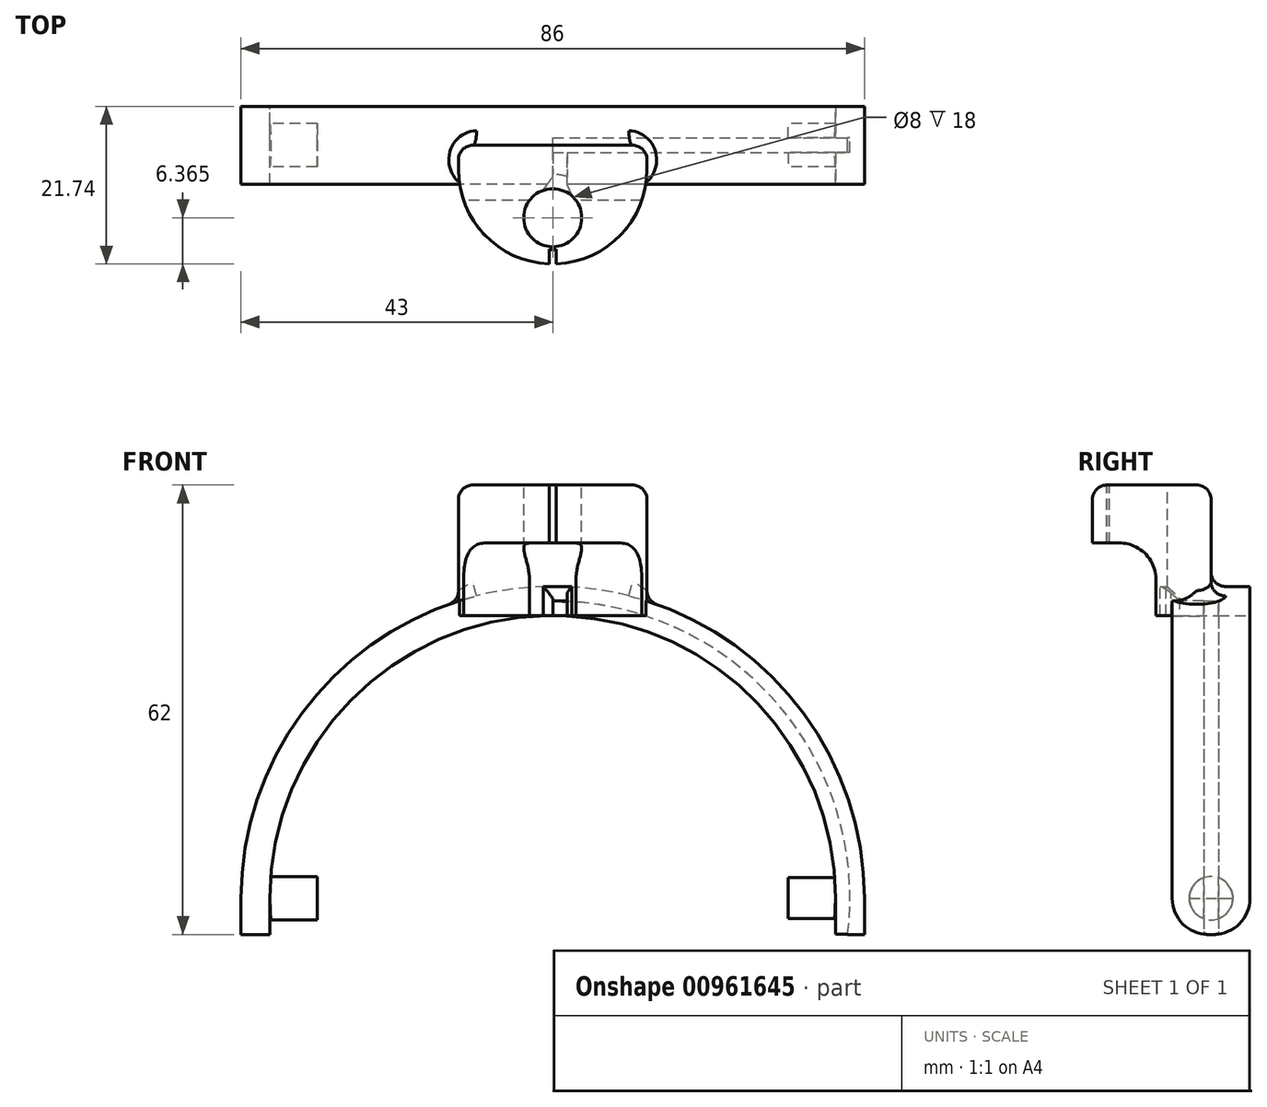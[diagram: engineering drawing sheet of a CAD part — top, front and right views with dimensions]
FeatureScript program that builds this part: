
annotation { "Feature Type Name" : "Feature", "Feature Type Description" : "" }
export const myFeature = defineFeature(function(context is Context, id is Id, definition is map)
    precondition{}
    {
        {
            var Q0;
            Q0=qCreatedBy(makeId("Front.planeOp"),FACE);
            var sketch = newSketch(context, id + "F0", { "sketchPlane" : qUnion([Q0])});
            skArc(sketch, "E0", {"start": v(39, 0) * mm, "mid": v(0, 39) * mm, "end": v(-39, 0) * mm});
            skArc(sketch, "E1", {"start": v(43, 0) * mm, "mid": v(0, 43) * mm, "end": v(-43, 0) * mm});
            skLineSegment(sketch, "E2", {"start": v(-43, 0) * mm, "end": v(-39, 0) * mm});
            skLineSegment(sketch, "E3", {"start": v(39, 0) * mm, "end": v(43, 0) * mm});
            skLineSegment(sketch, "E4", {"start": v(63.06, -5) * mm, "end": v(-58.13, -5) * mm, "construction": true});
            skLineSegment(sketch, "E5", {"start": v(43, 0) * mm, "end": v(43, -5) * mm});
            skLineSegment(sketch, "E6", {"start": v(43, -5) * mm, "end": v(39, -5) * mm});
            skLineSegment(sketch, "E7", {"start": v(39, -5) * mm, "end": v(39, 0) * mm});
            skLineSegment(sketch, "E8", {"start": v(-39, 0) * mm, "end": v(-39, -5) * mm});
            skLineSegment(sketch, "E9", {"start": v(-39, -5) * mm, "end": v(-43, -5) * mm});
            skLineSegment(sketch, "E10", {"start": v(-43, -5) * mm, "end": v(-43, 0) * mm});
            skSolve(sketch);
        }
        {
            var Q0;
            Q0=makeQuery(id+"F0.imprint","IMPRINT",FACE,{"disambiguationData":[TD([[makeQuery(id+"F0.imprint","IMPRINT",EDGE,{"derivedFrom":sQuery(id+"F0.wireOp",EDGE,"E0")}),-1.0]])]});
            var Q1;
            Q1=makeQuery(id+"F0.imprint","IMPRINT",FACE,{"disambiguationData":[TD([[makeQuery(id+"F0.imprint","IMPRINT",EDGE,{"derivedFrom":sQuery(id+"F0.wireOp",EDGE,"E3")}),-1.0]])]});
            var Q2;
            Q2=makeQuery(id+"F0.imprint","IMPRINT",FACE,{"disambiguationData":[TD([[makeQuery(id+"F0.imprint","IMPRINT",EDGE,{"derivedFrom":sQuery(id+"F0.wireOp",EDGE,"E2")}),-1.0]])]});
            extrude(context, id + "F1", {"entities" : qUnion([Q0, Q1, Q2]), "depth" : 10.75 * mm, "offsetDistance" : 25 * mm});
        }
        {
            var Q0;
            Q0=makeQuery(id+"F1.opExtrude","CAP_FACE",FACE,{"disambiguationData":[OSD([sQuery(id+"F0.wireOp",EDGE,"E0"),sQuery(id+"F0.wireOp",EDGE,"E1"),sQuery(id+"F0.wireOp",EDGE,"E2"),sQuery(id+"F0.wireOp",EDGE,"E3")])],"isStart":false});
            var sketch = newSketch(context, id + "F2", { "sketchPlane" : qUnion([Q0])});
            skLineSegment(sketch, "E11.bottom", {"start": v(-13, 57) * mm, "end": v(13, 57) * mm});
            skLineSegment(sketch, "E11.top", {"start": v(-13, 39) * mm, "end": v(13, 39) * mm});
            skLineSegment(sketch, "E11.left", {"start": v(-13, 57) * mm, "end": v(-13, 39) * mm});
            skLineSegment(sketch, "E11.right", {"start": v(13, 57) * mm, "end": v(13, 39) * mm});
            skSolve(sketch);
        }
        {
            var Q0;
            {var subQ0=sQuery(id+"F2.wireOp",EDGE,"E11.bottom");Q0=makeQuery(id+"F2.imprint","IMPRINT",FACE,{"disambiguationData":[TD([[makeQuery(id+"F2.imprint","IMPRINT",EDGE,{"derivedFrom":subQ0}),-1.0]])]});}
            var Q1;
            {var subQ0=sQuery(id+"F2.wireOp",EDGE,"E11.left");var subQ1=sQuery(id+"F2.wireOp",EDGE,"E11.top");var subQ2=makeQuery(id+"F2.imprint","INTERSECT",VERTEX,{"derivedFrom":[subQ1,subQ0]});Q1=makeQuery(id+"F2.imprint","IMPRINT",FACE,{"disambiguationData":[TD([[makeQuery(id+"F2.imprint","IMPRINT",EDGE,{"disambiguationData":[TD([[subQ2,-1.0]])],"derivedFrom":subQ1}),1.0]])]});}
            extrude(context, id + "F3", {"entities" : qUnion([Q0, Q1]), "operationType" : NewBodyOperationType.ADD, "depth" : 11 * mm, "offsetDistance" : 25 * mm, "hasSecondDirection" : true, "secondDirectionOppositeDirection" : true, "secondDirectionDepth" : 5.38 * mm});
        }
        {
            var Q0;
            Q0=makeQuery(id+"F3.opExtrude","CAP_EDGE",EDGE,{"disambiguationData":[OSD([sQuery(id+"F2.wireOp",EDGE,"E11.right")])],"isStart":false});
            var Q1;
            Q1=makeQuery(id+"F3.opExtrude","CAP_EDGE",EDGE,{"disambiguationData":[OSD([sQuery(id+"F2.wireOp",EDGE,"E11.left")])],"isStart":false});
            fillet(context, id + "F4", {"entities" : qUnion([Q0, Q1]), "radius" : 13 * mm, "tangentPropagation" : true, "defaultsChanged" : false, "vertexSettings" : [], "allowEdgeOverflow" : false});
        }
        {
            var Q0;
            Q0=makeQuery(id+"F3.opExtrude","SWEPT_FACE",FACE,{"disambiguationData":[OSD([sQuery(id+"F2.wireOp",EDGE,"E11.bottom")])]});
            var sketch = newSketch(context, id + "F5", { "sketchPlane" : qUnion([Q0])});
            skCircle(sketch, "E12", {"center": v(0, -15.38) * mm, "radius": 4 * mm});
            skSolve(sketch);
        }
        {
            var Q0;
            Q0=makeQuery(id+"F5.imprint","IMPRINT",FACE,{"disambiguationData":[TD([[makeQuery(id+"F5.imprint","IMPRINT",EDGE,{"derivedFrom":sQuery(id+"F5.wireOp",EDGE,"E12")}),1.0]])]});
            extrude(context, id + "F6", {"entities" : qUnion([Q0]), "operationType" : NewBodyOperationType.REMOVE, "oppositeDirection" : true, "depth" : 25 * mm, "offsetDistance" : 25 * mm});
        }
        {
            var Q0;
            {var subQ0=makeQuery(id+"F1.opExtrude","SWEPT_FACE",FACE,{"disambiguationData":[OSD([sQuery(id+"F0.wireOp",EDGE,"E1")])]});var subQ1=sQuery(id+"F2.wireOp",EDGE,"E11.left");var subQ2=makeQuery(id+"F3.opExtrude","CAP_FACE",FACE,{"disambiguationData":[OSD([sQuery(id+"F2.wireOp",EDGE,"E11.bottom"),sQuery(id+"F2.wireOp",EDGE,"E11.top"),subQ1,sQuery(id+"F2.wireOp",EDGE,"E11.right")])],"isStart":true});Q0=makeQuery(id+"FzuqFp6sAI3lxhp_1.boolean.opBoolean","SPLIT",EDGE,{"disambiguationData":[TD([makeQuery(id+"F3.opExtrude","SWEPT_FACE",FACE,{"disambiguationData":[OSD([subQ1])]})])],"derivedFrom":makeQuery(id+"F3.boolean.opBoolean","INTERSECT",EDGE,{"derivedFrom":[subQ0,subQ2]})});}
            var Q1;
            {var subQ0=makeQuery(id+"F1.opExtrude","SWEPT_FACE",FACE,{"disambiguationData":[OSD([sQuery(id+"F0.wireOp",EDGE,"E1")])]});var subQ1=sQuery(id+"F2.wireOp",EDGE,"E11.right");var subQ2=makeQuery(id+"F3.opExtrude","CAP_FACE",FACE,{"disambiguationData":[OSD([sQuery(id+"F2.wireOp",EDGE,"E11.bottom"),sQuery(id+"F2.wireOp",EDGE,"E11.top"),sQuery(id+"F2.wireOp",EDGE,"E11.left"),subQ1])],"isStart":true});Q1=makeQuery(id+"FzuqFp6sAI3lxhp_1.boolean.opBoolean","SPLIT",EDGE,{"disambiguationData":[TD([makeQuery(id+"F3.opExtrude","SWEPT_FACE",FACE,{"disambiguationData":[OSD([subQ1])]})])],"derivedFrom":makeQuery(id+"F3.boolean.opBoolean","INTERSECT",EDGE,{"derivedFrom":[subQ0,subQ2]})});}
            var Q2;
            Q2=makeQuery(id+"FzuqFp6sAI3lxhp_1.boolean.opBoolean","INTERSECT",EDGE,{"derivedFrom":[makeQuery(id+"F3.opExtrude","CAP_FACE",FACE,{"disambiguationData":[OSD([sQuery(id+"F2.wireOp",EDGE,"E11.bottom"),sQuery(id+"F2.wireOp",EDGE,"E11.top"),sQuery(id+"F2.wireOp",EDGE,"E11.left"),sQuery(id+"F2.wireOp",EDGE,"E11.right")])],"isStart":true}),makeQuery(id+"FzuqFp6sAI3lxhp_1.opExtrude","SWEPT_FACE",FACE,{"disambiguationData":[OSD([sQuery(id+"FRsUaT8Pyvrhzy0_1.wireOp",EDGE,"mObt9MSs-sKAg-swzv-7bB1-zA0te2DPEE11.right")])]})]});
            var Q3;
            Q3=makeQuery(id+"FzuqFp6sAI3lxhp_1.boolean.opBoolean","INTERSECT",EDGE,{"derivedFrom":[makeQuery(id+"F3.opExtrude","CAP_FACE",FACE,{"disambiguationData":[OSD([sQuery(id+"F2.wireOp",EDGE,"E11.bottom"),sQuery(id+"F2.wireOp",EDGE,"E11.top"),sQuery(id+"F2.wireOp",EDGE,"E11.left"),sQuery(id+"F2.wireOp",EDGE,"E11.right")])],"isStart":true}),makeQuery(id+"FzuqFp6sAI3lxhp_1.opExtrude","SWEPT_FACE",FACE,{"disambiguationData":[OSD([sQuery(id+"FRsUaT8Pyvrhzy0_1.wireOp",EDGE,"mObt9MSs-sKAg-swzv-7bB1-zA0te2DPEE11.top")])]})]});
            var Q4;
            Q4=makeQuery(id+"FzuqFp6sAI3lxhp_1.boolean.opBoolean","INTERSECT",EDGE,{"derivedFrom":[makeQuery(id+"F3.opExtrude","CAP_FACE",FACE,{"disambiguationData":[OSD([sQuery(id+"F2.wireOp",EDGE,"E11.bottom"),sQuery(id+"F2.wireOp",EDGE,"E11.top"),sQuery(id+"F2.wireOp",EDGE,"E11.left"),sQuery(id+"F2.wireOp",EDGE,"E11.right")])],"isStart":true}),makeQuery(id+"FzuqFp6sAI3lxhp_1.opExtrude","SWEPT_FACE",FACE,{"disambiguationData":[OSD([sQuery(id+"FRsUaT8Pyvrhzy0_1.wireOp",EDGE,"mObt9MSs-sKAg-swzv-7bB1-zA0te2DPEE11.left")])]})]});
            var Q5;
            Q5=makeQuery(id+"F3.opExtrude","CAP_EDGE",EDGE,{"disambiguationData":[OSD([sQuery(id+"F2.wireOp",EDGE,"E11.left")])],"isStart":true});
            var Q6;
            Q6=makeQuery(id+"F4.opFillet","BLEND_EDGE",EDGE,{"blendedFrom":[makeQuery(id+"F3.opExtrude","CAP_EDGE",EDGE,{"disambiguationData":[OSD([sQuery(id+"F2.wireOp",EDGE,"E11.left")])],"isStart":false}),makeQuery(id+"F3.opExtrude","SWEPT_FACE",FACE,{"disambiguationData":[OSD([sQuery(id+"F2.wireOp",EDGE,"E11.bottom")])]})],"blendedInto":[makeQuery(id+"F3.opExtrude","SWEPT_FACE",FACE,{"disambiguationData":[OSD([sQuery(id+"F2.wireOp",EDGE,"E11.bottom")])]})]});
            var Q7;
            Q7=makeQuery(id+"F3.opExtrude","CAP_EDGE",EDGE,{"disambiguationData":[OSD([sQuery(id+"F2.wireOp",EDGE,"E11.bottom")])],"isStart":true});
            var Q8;
            Q8=makeQuery(id+"F3.opExtrude","CAP_EDGE",EDGE,{"disambiguationData":[OSD([sQuery(id+"F2.wireOp",EDGE,"E11.right")])],"isStart":true});
            var Q9;
            Q9=makeQuery(id+"F4.opFillet","BLEND_EDGE",EDGE,{"blendedFrom":[makeQuery(id+"F3.opExtrude","CAP_EDGE",EDGE,{"disambiguationData":[OSD([sQuery(id+"F2.wireOp",EDGE,"E11.right")])],"isStart":false}),makeQuery(id+"FzuqFp6sAI3lxhp_1.boolean.opBoolean","COPY",FACE,{"derivedFrom":makeQuery(id+"FzuqFp6sAI3lxhp_1.opExtrude","SWEPT_FACE",FACE,{"disambiguationData":[OSD([sQuery(id+"FRsUaT8Pyvrhzy0_1.wireOp",EDGE,"mObt9MSs-sKAg-swzv-7bB1-zA0te2DPEE11.top")])]})})],"blendedInto":[makeQuery(id+"FzuqFp6sAI3lxhp_1.boolean.opBoolean","COPY",FACE,{"derivedFrom":makeQuery(id+"FzuqFp6sAI3lxhp_1.opExtrude","SWEPT_FACE",FACE,{"disambiguationData":[OSD([sQuery(id+"FRsUaT8Pyvrhzy0_1.wireOp",EDGE,"mObt9MSs-sKAg-swzv-7bB1-zA0te2DPEE11.top")])]})})]});
            var Q10;
            Q10=makeQuery(id+"F4.opFillet","BLEND_EDGE",EDGE,{"blendedFrom":[makeQuery(id+"F3.opExtrude","CAP_EDGE",EDGE,{"disambiguationData":[OSD([sQuery(id+"F2.wireOp",EDGE,"E11.right")])],"isStart":false}),makeQuery(id+"FzuqFp6sAI3lxhp_1.boolean.opBoolean","COPY",FACE,{"derivedFrom":makeQuery(id+"FzuqFp6sAI3lxhp_1.opExtrude","SWEPT_FACE",FACE,{"disambiguationData":[OSD([sQuery(id+"FRsUaT8Pyvrhzy0_1.wireOp",EDGE,"mObt9MSs-sKAg-swzv-7bB1-zA0te2DPEE11.right")])]})})],"blendedInto":[makeQuery(id+"FzuqFp6sAI3lxhp_1.boolean.opBoolean","COPY",FACE,{"derivedFrom":makeQuery(id+"FzuqFp6sAI3lxhp_1.opExtrude","SWEPT_FACE",FACE,{"disambiguationData":[OSD([sQuery(id+"FRsUaT8Pyvrhzy0_1.wireOp",EDGE,"mObt9MSs-sKAg-swzv-7bB1-zA0te2DPEE11.right")])]})})]});
            var Q11;
            Q11=makeQuery(id+"F4.opFillet","BLEND_EDGE",EDGE,{"blendedFrom":[makeQuery(id+"F3.opExtrude","CAP_EDGE",EDGE,{"disambiguationData":[OSD([sQuery(id+"F2.wireOp",EDGE,"E11.left")])],"isStart":false}),makeQuery(id+"FzuqFp6sAI3lxhp_1.boolean.opBoolean","COPY",FACE,{"derivedFrom":makeQuery(id+"FzuqFp6sAI3lxhp_1.opExtrude","SWEPT_FACE",FACE,{"disambiguationData":[OSD([sQuery(id+"FRsUaT8Pyvrhzy0_1.wireOp",EDGE,"mObt9MSs-sKAg-swzv-7bB1-zA0te2DPEE11.left")])]})})],"blendedInto":[makeQuery(id+"FzuqFp6sAI3lxhp_1.boolean.opBoolean","COPY",FACE,{"derivedFrom":makeQuery(id+"FzuqFp6sAI3lxhp_1.opExtrude","SWEPT_FACE",FACE,{"disambiguationData":[OSD([sQuery(id+"FRsUaT8Pyvrhzy0_1.wireOp",EDGE,"mObt9MSs-sKAg-swzv-7bB1-zA0te2DPEE11.left")])]})})]});
            fillet(context, id + "F7", {"entities" : qUnion([Q0, Q1, Q2, Q3, Q4, Q5, Q6, Q7, Q8, Q9, Q10, Q11]), "radius" : 2 * mm, "tangentPropagation" : true, "defaultsChanged" : false, "vertexSettings" : [], "allowEdgeOverflow" : false});
        }
        {
            var Q0;
            Q0=qCreatedBy(makeId("Right.planeOp"),FACE);
            var sketch = newSketch(context, id + "F8", { "sketchPlane" : qUnion([Q0])});
            skLineSegment(sketch, "E13.bottom", {"start": v(-13, 35.02) * mm, "end": v(-25, 35.02) * mm});
            skLineSegment(sketch, "E13.top", {"start": v(-18, 49) * mm, "end": v(-25, 49) * mm});
            skLineSegment(sketch, "E13.left", {"start": v(-13, 35.02) * mm, "end": v(-13, 44) * mm});
            skLineSegment(sketch, "E13.right", {"start": v(-25, 35.02) * mm, "end": v(-25, 49) * mm});
            skPoint(sketch, "E14.visualSharp", {"position": v(-13, 49) * mm});
            skArc(sketch, "E14.filletArc", {"start": v(-13, 44) * mm, "mid": v(-14.46, 47.54) * mm, "end": v(-18, 49) * mm});
            skSolve(sketch);
        }
        {
            var Q0;
            Q0=makeQuery(id+"F8.imprint","IMPRINT",FACE,{"disambiguationData":[TD([[makeQuery(id+"F8.imprint","IMPRINT",EDGE,{"derivedFrom":sQuery(id+"F8.wireOp",EDGE,"E13.bottom")}),-1.0]])]});
            extrude(context, id + "F9", {"entities" : qUnion([Q0]), "operationType" : NewBodyOperationType.REMOVE, "oppositeDirection" : true, "depth" : 25 * mm, "offsetDistance" : 25 * mm, "hasSecondDirection" : true, "secondDirectionOppositeDirection" : false, "secondDirectionDepth" : 25 * mm});
        }
        {
            var Q0;
            Q0=qCreatedBy(makeId("Right.planeOp"),FACE);
            var sketch = newSketch(context, id + "F10", { "sketchPlane" : qUnion([Q0])});
            skCircle(sketch, "E15", {"center": v(-5.38, 0) * mm, "radius": 3 * mm});
            skSolve(sketch);
        }
        {
            var Q0;
            Q0=makeQuery(id+"F10.imprint","IMPRINT",FACE,{"disambiguationData":[TD([[makeQuery(id+"F10.imprint","IMPRINT",EDGE,{"derivedFrom":sQuery(id+"F10.wireOp",EDGE,"E15")}),1.0]])]});
            var Q1;
            {var subQ2=sQuery(id+"F0.wireOp",EDGE,"E8");var subQ7=sQuery(id+"F0.wireOp",EDGE,"E0");Q1=makeQuery(id+"FzuqFp6sAI3lxhp_1.boolean.opBoolean","SPLIT",FACE,{"disambiguationData":[TD([makeQuery(id+"F1.opExtrude","SWEPT_FACE",FACE,{"disambiguationData":[OSD([subQ2])]})])],"derivedFrom":makeQuery(id+"F1.opExtrude","SWEPT_FACE",FACE,{"disambiguationData":[OSD([subQ7])]})});}
            var Q2;
            {var subQ2=sQuery(id+"F0.wireOp",EDGE,"E8");var subQ7=sQuery(id+"F0.wireOp",EDGE,"E0");Q2=makeQuery(id+"FzuqFp6sAI3lxhp_1.boolean.opBoolean","SPLIT",FACE,{"disambiguationData":[TD([makeQuery(id+"F1.opExtrude","SWEPT_FACE",FACE,{"disambiguationData":[OSD([subQ2])]})])],"derivedFrom":makeQuery(id+"F1.opExtrude","SWEPT_FACE",FACE,{"disambiguationData":[OSD([subQ7])]})});}
            extrude(context, id + "F11", {"entities" : qUnion([Q0]), "operationType" : NewBodyOperationType.ADD, "endBound" : BoundingType.UP_TO_SURFACE, "depth" : 25 * mm, "endBoundEntityFace" : qUnion([Q1]), "offsetDistance" : 25 * mm, "hasSecondDirection" : true, "secondDirectionBound" : SecondDirectionBoundingType.UP_TO_SURFACE, "secondDirectionOppositeDirection" : true, "secondDirectionDepth" : 25 * mm, "secondDirectionBoundEntityFace" : qUnion([Q2])});
        }
        {
            var Q0;
            Q0=qCreatedBy(makeId("Front.planeOp"),FACE);
            var sketch = newSketch(context, id + "F12", { "sketchPlane" : qUnion([Q0])});
            skLineSegment(sketch, "E16.bottom", {"start": v(-32.5, 7) * mm, "end": v(32.5, 7) * mm});
            skLineSegment(sketch, "E16.top", {"start": v(-32.5, -8) * mm, "end": v(32.5, -8) * mm});
            skLineSegment(sketch, "E16.left", {"start": v(-32.5, 7) * mm, "end": v(-32.5, -8) * mm});
            skLineSegment(sketch, "E16.right", {"start": v(32.5, 7) * mm, "end": v(32.5, -8) * mm});
            skSolve(sketch);
        }
        {
            var Q0;
            Q0=makeQuery(id+"F12.imprint","IMPRINT",FACE,{"disambiguationData":[TD([[makeQuery(id+"F12.imprint","IMPRINT",EDGE,{"derivedFrom":sQuery(id+"F12.wireOp",EDGE,"E16.bottom")}),-1.0]])]});
            extrude(context, id + "F13", {"entities" : qUnion([Q0]), "operationType" : NewBodyOperationType.REMOVE, "depth" : 10 * mm, "offsetDistance" : 25 * mm});
        }
        {
            var Q0;
            Q0=makeQuery(id+"F1.opExtrude","CAP_EDGE",EDGE,{"disambiguationData":[OSD([sQuery(id+"F0.wireOp",EDGE,"E9")])],"isStart":false});
            var Q1;
            Q1=makeQuery(id+"F1.opExtrude","CAP_EDGE",EDGE,{"disambiguationData":[OSD([sQuery(id+"F0.wireOp",EDGE,"E9")])],"isStart":true});
            var Q2;
            Q2=makeQuery(id+"F1.opExtrude","CAP_EDGE",EDGE,{"disambiguationData":[OSD([sQuery(id+"F0.wireOp",EDGE,"E6")])],"isStart":false});
            var Q3;
            Q3=makeQuery(id+"F1.opExtrude","CAP_EDGE",EDGE,{"disambiguationData":[OSD([sQuery(id+"F0.wireOp",EDGE,"E6")])],"isStart":true});
            fillet(context, id + "F14", {"entities" : qUnion([Q0, Q1, Q2, Q3]), "tangentPropagation" : true, "radius" : 5 * mm, "defaultsChanged" : false, "vertexSettings" : [], "allowEdgeOverflow" : false});
        }
        {
            var Q0;
            Q0=qCreatedBy(makeId("Top.planeOp"),FACE);
            var sketch = newSketch(context, id + "F15", { "sketchPlane" : qUnion([Q0])});
            skLineSegment(sketch, "E17", {"start": v(-40.37, -5.38) * mm, "end": v(52.89, -5.38) * mm, "construction": true});
            skLineSegment(sketch, "E18.bottom", {"start": v(32.5, -6.37) * mm, "end": v(41, -6.37) * mm});
            skLineSegment(sketch, "E18.top", {"start": v(32.5, -4.37) * mm, "end": v(41, -4.37) * mm});
            skLineSegment(sketch, "E18.left", {"start": v(32.5, -6.37) * mm, "end": v(32.5, -4.37) * mm});
            skLineSegment(sketch, "E18.right", {"start": v(41, -6.37) * mm, "end": v(41, -4.37) * mm});
            skLineSegment(sketch, "E19", {"start": v(0, 14.24) * mm, "end": v(0, -26.41) * mm, "construction": true});
            skSolve(sketch);
        }
        {
            var Q0;
            Q0=qSketchRegion(id+"F15",true);
            var Q1;
            Q1=sQuery(id+"F15.wireOp",EDGE,"E19");
            revolve(context, id + "F16", {"operationType" : NewBodyOperationType.REMOVE, "surfaceOperationType" : NewSurfaceOperationType.NEW, "entities" : qUnion([Q0]), "axis" : qUnion([Q1]), "revolveType" : RevolveType.SYMMETRIC, "angle" : 180 * degree});
        }
        {
            var Q0;
            Q0=qCreatedBy(makeId("Top.planeOp"),FACE);
            cPlane(context, id + "F17", {"entities" : qUnion([Q0]), "cplaneType" : CPlaneType.OFFSET, "offset" : 39 * mm, "width" : 150 * mm, "height" : 150 * mm});
        }
        {
            var Q0;
            Q0=qCreatedBy(id+"F17.planeOp",FACE);
            var sketch = newSketch(context, id + "F18", { "sketchPlane" : qUnion([Q0])});
            skLineSegment(sketch, "E20.bottom", {"start": v(0, -6.37) * mm, "end": v(2, -6.37) * mm});
            skLineSegment(sketch, "E20.top", {"start": v(0, -14.37) * mm, "end": v(2, -14.37) * mm});
            skLineSegment(sketch, "E20.left", {"start": v(0, -6.37) * mm, "end": v(0, -14.37) * mm});
            skLineSegment(sketch, "E20.right", {"start": v(2, -6.37) * mm, "end": v(2, -14.37) * mm});
            skSolve(sketch);
        }
        {
            var Q0;
            Q0=makeQuery(id+"F18.imprint","IMPRINT",FACE,{"disambiguationData":[TD([[makeQuery(id+"F18.imprint","IMPRINT",EDGE,{"derivedFrom":sQuery(id+"F18.wireOp",EDGE,"E20.bottom")}),-1.0]])]});
            extrude(context, id + "F19", {"entities" : qUnion([Q0]), "operationType" : NewBodyOperationType.REMOVE, "oppositeDirection" : true, "depth" : 2 * mm, "offsetDistance" : 25 * mm, "hasSecondDirection" : true, "secondDirectionOppositeDirection" : false, "secondDirectionDepth" : 2 * mm});
        }
        {
            var Q0;
            Q0=makeQuery(id+"F19.boolean.opBoolean","INTERSECT",EDGE,{"derivedFrom":[makeQuery(id+"F6.boolean.opBoolean","COPY",FACE,{"derivedFrom":makeQuery(id+"F6.opExtrude","SWEPT_FACE",FACE,{"disambiguationData":[OSD([sQuery(id+"F5.wireOp",EDGE,"E12")])]})}),makeQuery(id+"F19.opExtrude","CAP_FACE",FACE,{"disambiguationData":[OSD([sQuery(id+"F18.wireOp",EDGE,"E20.bottom"),sQuery(id+"F18.wireOp",EDGE,"E20.top"),sQuery(id+"F18.wireOp",EDGE,"E20.left"),sQuery(id+"F18.wireOp",EDGE,"E20.right")])],"isStart":true})]});
            var Q1;
            Q1=makeQuery(id+"F19.boolean.opBoolean","INTERSECT",EDGE,{"derivedFrom":[makeQuery(id+"F6.boolean.opBoolean","COPY",FACE,{"derivedFrom":makeQuery(id+"F6.opExtrude","SWEPT_FACE",FACE,{"disambiguationData":[OSD([sQuery(id+"F5.wireOp",EDGE,"E12")])]})}),makeQuery(id+"F19.opExtrude","SWEPT_FACE",FACE,{"disambiguationData":[OSD([sQuery(id+"F18.wireOp",EDGE,"E20.left")])]})]});
            var Q2;
            Q2=makeQuery(id+"F19.boolean.opBoolean","INTERSECT",EDGE,{"derivedFrom":[makeQuery(id+"F6.boolean.opBoolean","COPY",FACE,{"derivedFrom":makeQuery(id+"F6.opExtrude","SWEPT_FACE",FACE,{"disambiguationData":[OSD([sQuery(id+"F5.wireOp",EDGE,"E12")])]})}),makeQuery(id+"F19.opExtrude","SWEPT_FACE",FACE,{"disambiguationData":[OSD([sQuery(id+"F18.wireOp",EDGE,"E20.right")])]})]});
            chamfer(context, id + "F20", {"entities" : qUnion([Q0, Q1, Q2]), "width" : 2 * mm, "tangentPropagation" : true});
        }
        {
            var Q0;
            Q0=makeQuery(id+"F3.opExtrude","SWEPT_FACE",FACE,{"disambiguationData":[OSD([sQuery(id+"F2.wireOp",EDGE,"E11.bottom")])]});
            var sketch = newSketch(context, id + "F21", { "sketchPlane" : qUnion([Q0])});
            skLineSegment(sketch, "E21.bottom", {"start": v(-0.5, -18) * mm, "end": v(0.5, -18) * mm});
            skLineSegment(sketch, "E21.top", {"start": v(-0.5, -26) * mm, "end": v(0.5, -26) * mm});
            skLineSegment(sketch, "E21.left", {"start": v(-0.5, -18) * mm, "end": v(-0.5, -26) * mm});
            skLineSegment(sketch, "E21.right", {"start": v(0.5, -18) * mm, "end": v(0.5, -26) * mm});
            skSolve(sketch);
        }
        {
            var Q0;
            {var subQ0=sQuery(id+"F21.wireOp",EDGE,"E21.top");Q0=makeQuery(id+"F21.imprint","IMPRINT",FACE,{"disambiguationData":[TD([[makeQuery(id+"F21.imprint","IMPRINT",EDGE,{"derivedFrom":subQ0}),1.0]])]});}
            var Q1;
            {var subQ0=sQuery(id+"F21.wireOp",EDGE,"E21.bottom");Q1=makeQuery(id+"F21.imprint","IMPRINT",FACE,{"disambiguationData":[TD([[makeQuery(id+"F21.imprint","IMPRINT",EDGE,{"derivedFrom":subQ0}),-1.0]])]});}
            var Q2;
            {var subQ0=sQuery(id+"F21.wireOp",EDGE,"E21.left");var subQ4=makeQuery(id+"F6.boolean.opBoolean","COPY",EDGE,{"derivedFrom":makeQuery(id+"F6.opExtrude","CAP_EDGE",EDGE,{"disambiguationData":[OSD([sQuery(id+"F5.wireOp",EDGE,"E12")])],"isStart":true})});var subQ5=makeQuery(id+"F21.imprint","INTERSECT",VERTEX,{"derivedFrom":[subQ4,subQ0]});Q2=makeQuery(id+"F21.imprint","IMPRINT",FACE,{"disambiguationData":[TD([[makeQuery(id+"F21.imprint","IMPRINT",EDGE,{"disambiguationData":[TD([[subQ5,-1.0]])],"derivedFrom":subQ4}),-1.0]])]});}
            extrude(context, id + "F22", {"entities" : qUnion([Q0, Q1, Q2]), "operationType" : NewBodyOperationType.REMOVE, "oppositeDirection" : true, "depth" : 25 * mm, "offsetDistance" : 25 * mm});
        }
    });
